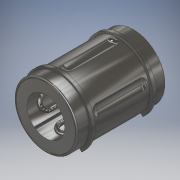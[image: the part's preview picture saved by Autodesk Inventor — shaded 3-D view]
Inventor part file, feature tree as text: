
AUTODESK INVENTOR PART (.ipt)
format: ipt  version: 2019 (Build 230136000, 136)  size: 1,591,808 bytes
history: native  units: in
note: dims shown in document units (in); Inventor stores cm internally (conversion verified against a paired STEP export)
features: extrude x2, direct_edit x1, fillet x1, move_body x1
ambient origin geometry x8: Origin, YZ Plane, XZ Plane, XY Plane, X Axis, Y Axis, Z Axis, Center Point
bodies: Solid1 (feature_tree), Solid2 (feature_tree), Solid3 (feature_tree)
feature tree (5):
  direct_edit  "Direct Edit1"
  fillet  "Fillet5"  Radius=0.839in
  extrude  "Extrude5"  [1 undecoded]
  extrude  "Extrude6"  [1 undecoded]
  move_body  "Move1"
note: 2 required parameter values undecoded (feature->parameter linkage not recoverable at this tier; creation-order binding heuristic only, values carry confidence <= 0.55)
